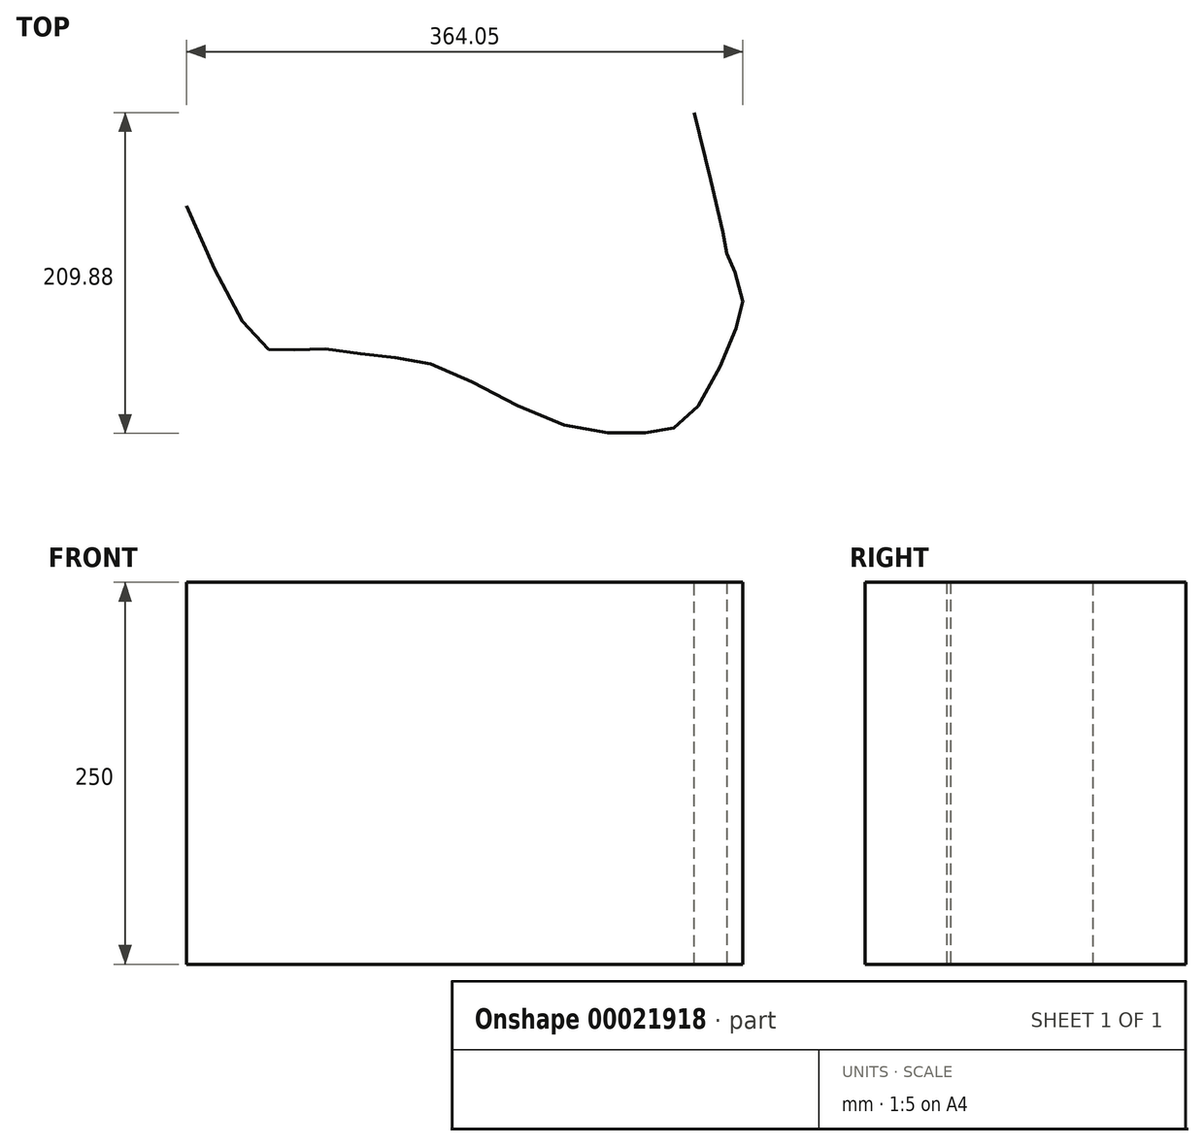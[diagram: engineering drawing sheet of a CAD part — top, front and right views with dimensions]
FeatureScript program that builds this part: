
annotation { "Feature Type Name" : "Feature", "Feature Type Description" : "" }
export const myFeature = defineFeature(function(context is Context, id is Id, definition is map)
    precondition{}
    {
        {
            var Q0;
            Q0=qCreatedBy(makeId("Top.planeOp"),FACE);
            var sketch = newSketch(context, id + "F0", { "sketchPlane" : qUnion([Q0])});
            skFitSpline(sketch, "E0", {"points": [v(-113.27, 0) * mm, v(-59.91, -93.9) * mm, v(-35.2, -93.44) * mm, v(6.72, -97.93) * mm, v(51.28, -105.15) * mm, v(128.96, -142.14) * mm, v(187.5, -148.73) * mm, v(214.97, -139.25) * mm, v(245.03, -83.63) * mm, v(249.99, -56.32) * mm, v(240.3, -32.16) * mm, v(240.17, -30.1) * mm, v(219.04, 60.79) * mm], "startDerivative": vector(427.28, -989.5) * mm, "endDerivative": vector(-260.1, 1051.63) * mm});
            skSolve(sketch);
        }
        {
            var Q0;
            Q0=sQuery(id+"F0.wireOp",EDGE,"E0");
            extrude(context, id + "F1", {"bodyType" : ToolBodyType.SURFACE, "surfaceEntities" : qUnion([Q0]), "depth" : 250 * mm});
        }
    });
